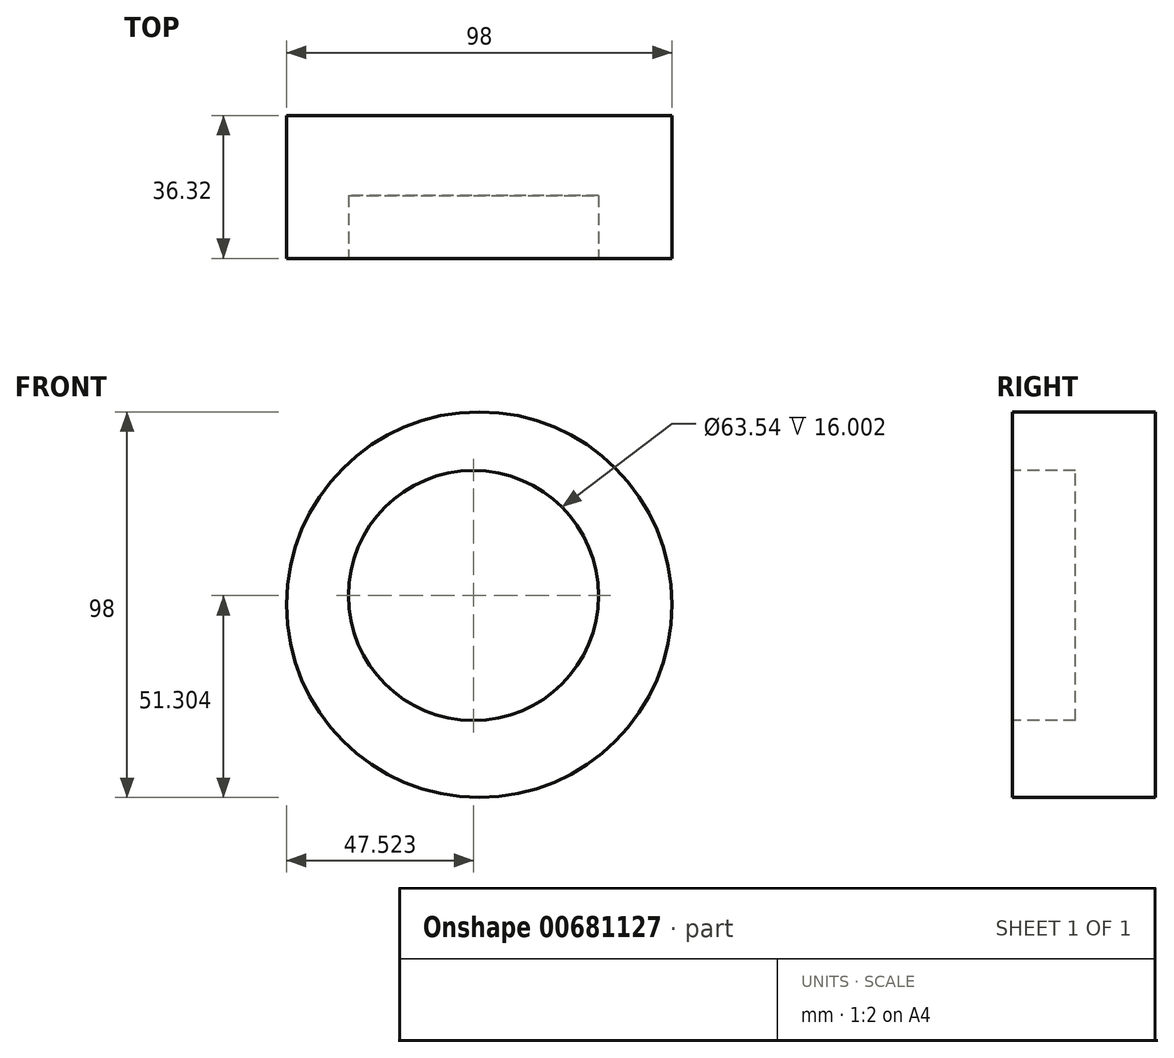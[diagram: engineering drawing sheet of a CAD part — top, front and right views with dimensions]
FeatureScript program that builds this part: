
annotation { "Feature Type Name" : "Feature", "Feature Type Description" : "" }
export const myFeature = defineFeature(function(context is Context, id is Id, definition is map)
    precondition{}
    {
        {
            var Q0;
            Q0=qCreatedBy(makeId("Front.planeOp"),FACE);
            var sketch = newSketch(context, id + "F0", { "sketchPlane" : qUnion([Q0])});
            skCircle(sketch, "E0", {"center": v(-15.11, 20.7) * mm, "radius": 49 * mm});
            skSolve(sketch);
        }
        {
            var Q0;
            Q0=makeQuery(id+"F0.imprint","IMPRINT",FACE,{"disambiguationData":[TD([[makeQuery(id+"F0.imprint","IMPRINT",EDGE,{"derivedFrom":sQuery(id+"F0.wireOp",EDGE,"E0")}),1.0]])]});
            extrude(context, id + "F1", {"entities" : qUnion([Q0]), "depth" : 50.8 * mm, "offsetDistance" : 25.4 * mm});
        }
        {
            var Q0;
            Q0=makeQuery(id+"F1.opExtrude","CAP_FACE",FACE,{"disambiguationData":[OSD([sQuery(id+"F0.wireOp",EDGE,"E0")])],"isStart":false});
            extrude(context, id + "F2", {"entities" : qUnion([Q0]), "operationType" : NewBodyOperationType.REMOVE, "oppositeDirection" : true, "depth" : 14.48 * mm, "offsetDistance" : 25.4 * mm});
        }
        {
            var Q0;
            Q0=makeQuery(id+"F2.boolean.opBoolean","COPY",FACE,{"derivedFrom":makeQuery(id+"F2.opExtrude","CAP_FACE",FACE,{"disambiguationData":[OSD([sQuery(id+"F0.wireOp",EDGE,"E0")])],"isStart":false})});
            var sketch = newSketch(context, id + "F3", { "sketchPlane" : qUnion([Q0])});
            skCircle(sketch, "E1", {"center": v(-16.59, 23) * mm, "radius": 31.77 * mm});
            skSolve(sketch);
        }
        {
            var Q0;
            Q0=makeQuery(id+"F3.imprint","IMPRINT",FACE,{"disambiguationData":[TD([[makeQuery(id+"F3.imprint","IMPRINT",EDGE,{"derivedFrom":sQuery(id+"F3.wireOp",EDGE,"E1")}),1.0]])]});
            extrude(context, id + "F4", {"entities" : qUnion([Q0]), "operationType" : NewBodyOperationType.REMOVE, "oppositeDirection" : true, "depth" : 16 * mm, "offsetDistance" : 25.4 * mm});
        }
    });
